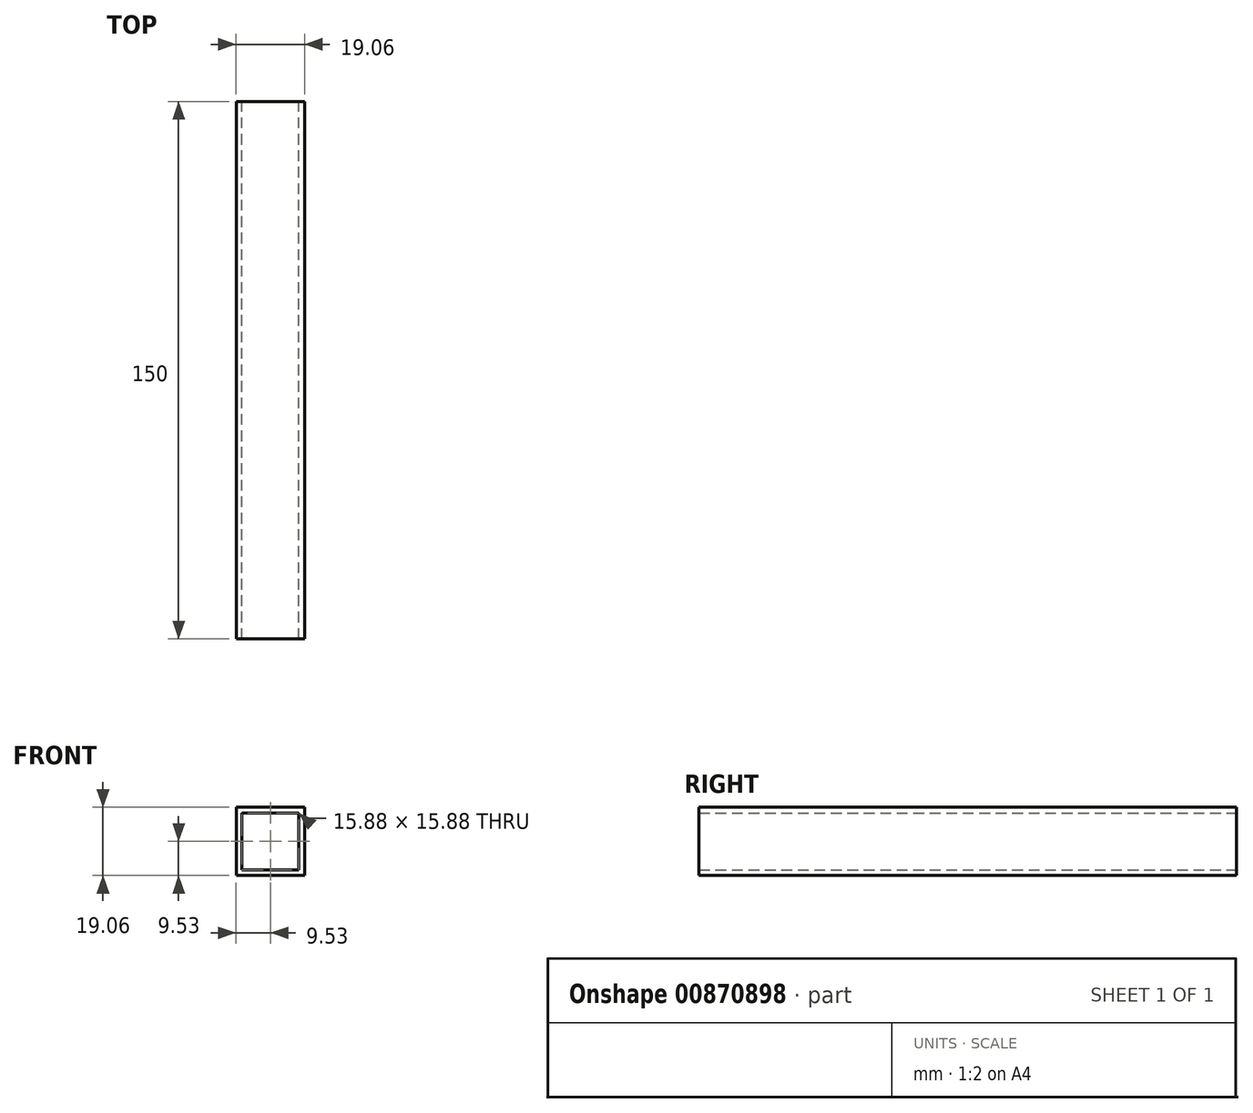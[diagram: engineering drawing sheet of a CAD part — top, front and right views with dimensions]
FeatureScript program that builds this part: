
annotation { "Feature Type Name" : "Feature", "Feature Type Description" : "" }
export const myFeature = defineFeature(function(context is Context, id is Id, definition is map)
    precondition{}
    {
        {
            var Q0;
            Q0=qCreatedBy(makeId("Front.planeOp"),FACE);
            var sketch = newSketch(context, id + "F0", { "sketchPlane" : qUnion([Q0])});
            skLineSegment(sketch, "E0.bottom", {"start": v(9.53, 9.53) * mm, "end": v(-9.53, 9.53) * mm});
            skLineSegment(sketch, "E0.top", {"start": v(9.53, -9.52) * mm, "end": v(-9.53, -9.52) * mm});
            skLineSegment(sketch, "E0.left", {"start": v(9.53, 9.53) * mm, "end": v(9.53, -9.52) * mm});
            skLineSegment(sketch, "E0.right", {"start": v(-9.53, 9.53) * mm, "end": v(-9.53, -9.52) * mm});
            skPoint(sketch, "E0.middle", {"position": v(0, 0) * mm});
            skLineSegment(sketch, "E1.bottom", {"start": v(7.94, 7.94) * mm, "end": v(-7.94, 7.94) * mm});
            skLineSegment(sketch, "E1.top", {"start": v(7.94, -7.94) * mm, "end": v(-7.94, -7.94) * mm});
            skLineSegment(sketch, "E1.left", {"start": v(7.94, 7.94) * mm, "end": v(7.94, -7.94) * mm});
            skLineSegment(sketch, "E1.right", {"start": v(-7.94, 7.94) * mm, "end": v(-7.94, -7.94) * mm});
            skSolve(sketch);
        }
        {
            var Q0;
            Q0 = qSketchRegion(id + "F0", true);
            extrude(context, id + "F1", {"entities" : qUnion([Q0]), "depth" : 150 * mm, "offsetDistance" : 25 * mm});
        }
    });
